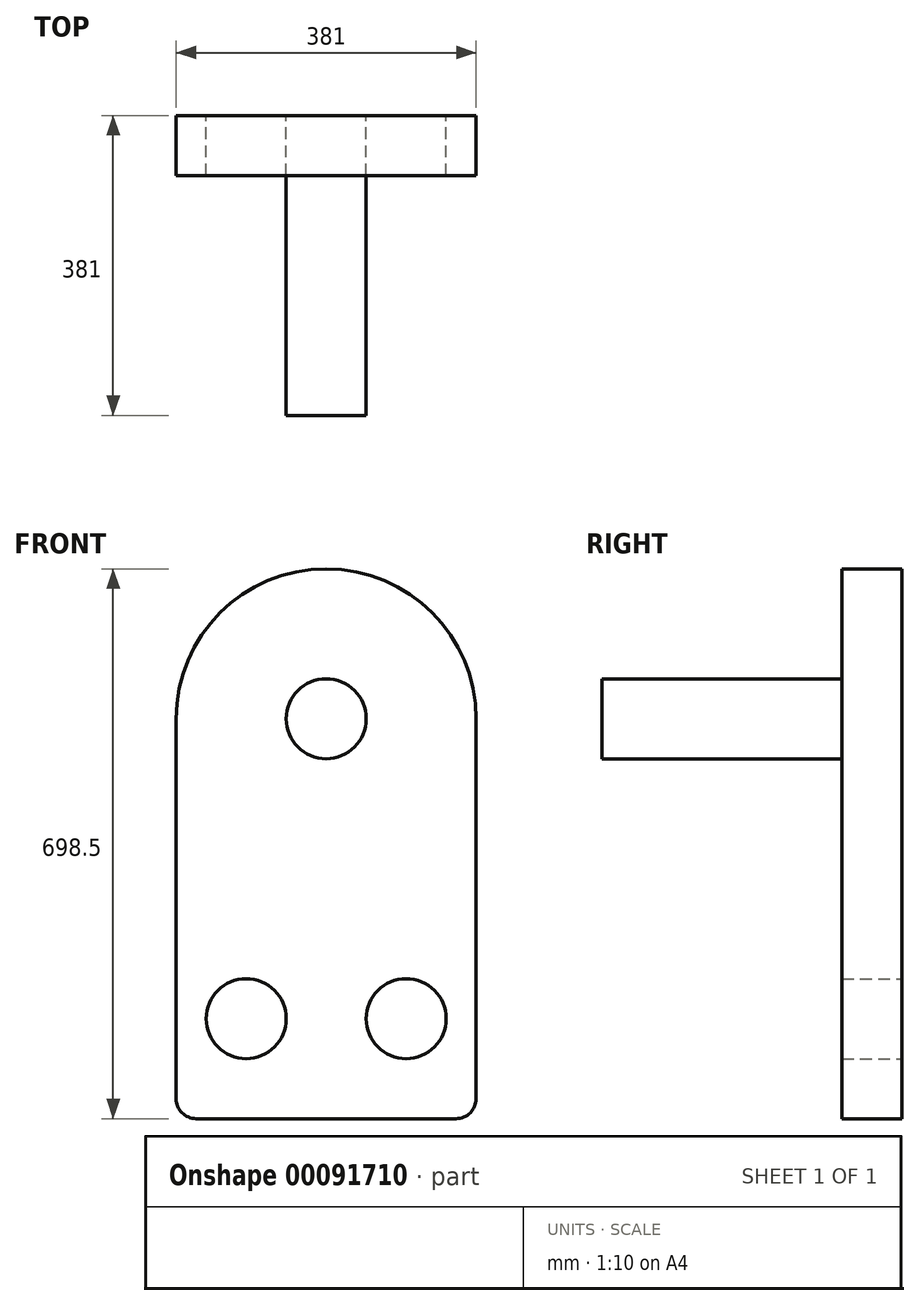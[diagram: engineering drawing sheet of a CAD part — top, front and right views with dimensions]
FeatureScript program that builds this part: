
annotation { "Feature Type Name" : "Feature", "Feature Type Description" : "" }
export const myFeature = defineFeature(function(context is Context, id is Id, definition is map)
    precondition{}
    {
        {
            var Q0;
            Q0=qCreatedBy(makeId("Front.planeOp"),FACE);
            var sketch = newSketch(context, id + "F0", { "sketchPlane" : qUnion([Q0])});
            skLineSegment(sketch, "E0.bottom", {"start": v(0, 0) * mm, "end": v(-381, 0) * mm});
            skLineSegment(sketch, "E0.left", {"start": v(0, 0) * mm, "end": v(0, 508) * mm});
            skLineSegment(sketch, "E0.right", {"start": v(-381, 0) * mm, "end": v(-381, 508) * mm});
            skArc(sketch, "E1", {"start": v(0, 508) * mm, "mid": v(-190.5, 698.5) * mm, "end": v(-381, 508) * mm});
            skCircle(sketch, "E2", {"center": v(-190.5, 508) * mm, "radius": 50.8 * mm});
            skCircle(sketch, "E3", {"center": v(-292.1, 127) * mm, "radius": 50.8 * mm});
            skCircle(sketch, "E4", {"center": v(-88.9, 127) * mm, "radius": 50.8 * mm});
            skLineSegment(sketch, "E5", {"start": v(-190.5, 508) * mm, "end": v(-190.5, 105.14) * mm, "construction": true});
            skLineSegment(sketch, "E6", {"start": v(-292.1, 127) * mm, "end": v(-88.9, 127) * mm, "construction": true});
            skSolve(sketch);
        }
        {
            var Q0;
            Q0=qSketchRegion(id+"F0",true);
            extrude(context, id + "F1", {"entities" : qUnion([Q0]), "depth" : 76.2 * mm});
        }
        {
            var Q0;
            Q0=makeQuery(id+"F0.imprint","IMPRINT",FACE,{"disambiguationData":[TD([[makeQuery(id+"F0.imprint","IMPRINT",EDGE,{"derivedFrom":sQuery(id+"F0.wireOp",EDGE,"E2")}),1.0]])]});
            extrude(context, id + "F2", {"entities" : qUnion([Q0]), "operationType" : NewBodyOperationType.ADD, "depth" : 381 * mm});
        }
        {
            var Q0;
            Q0=makeQuery(id+"F1.opExtrude","SWEPT_EDGE",EDGE,{"disambiguationData":[OSD([sQuery(id+"F0.wireOp",EDGE,"E0.bottom"),sQuery(id+"F0.wireOp",EDGE,"E0.right")])]});
            var Q1;
            Q1=makeQuery(id+"F1.opExtrude","SWEPT_EDGE",EDGE,{"disambiguationData":[OSD([sQuery(id+"F0.wireOp",EDGE,"E0.bottom"),sQuery(id+"F0.wireOp",EDGE,"E0.left")])]});
            fillet(context, id + "F3", {"entities" : qUnion([Q0, Q1]), "radius" : 25.4 * mm, "tangentPropagation" : true, "allowEdgeOverflow" : false});
        }
    });
